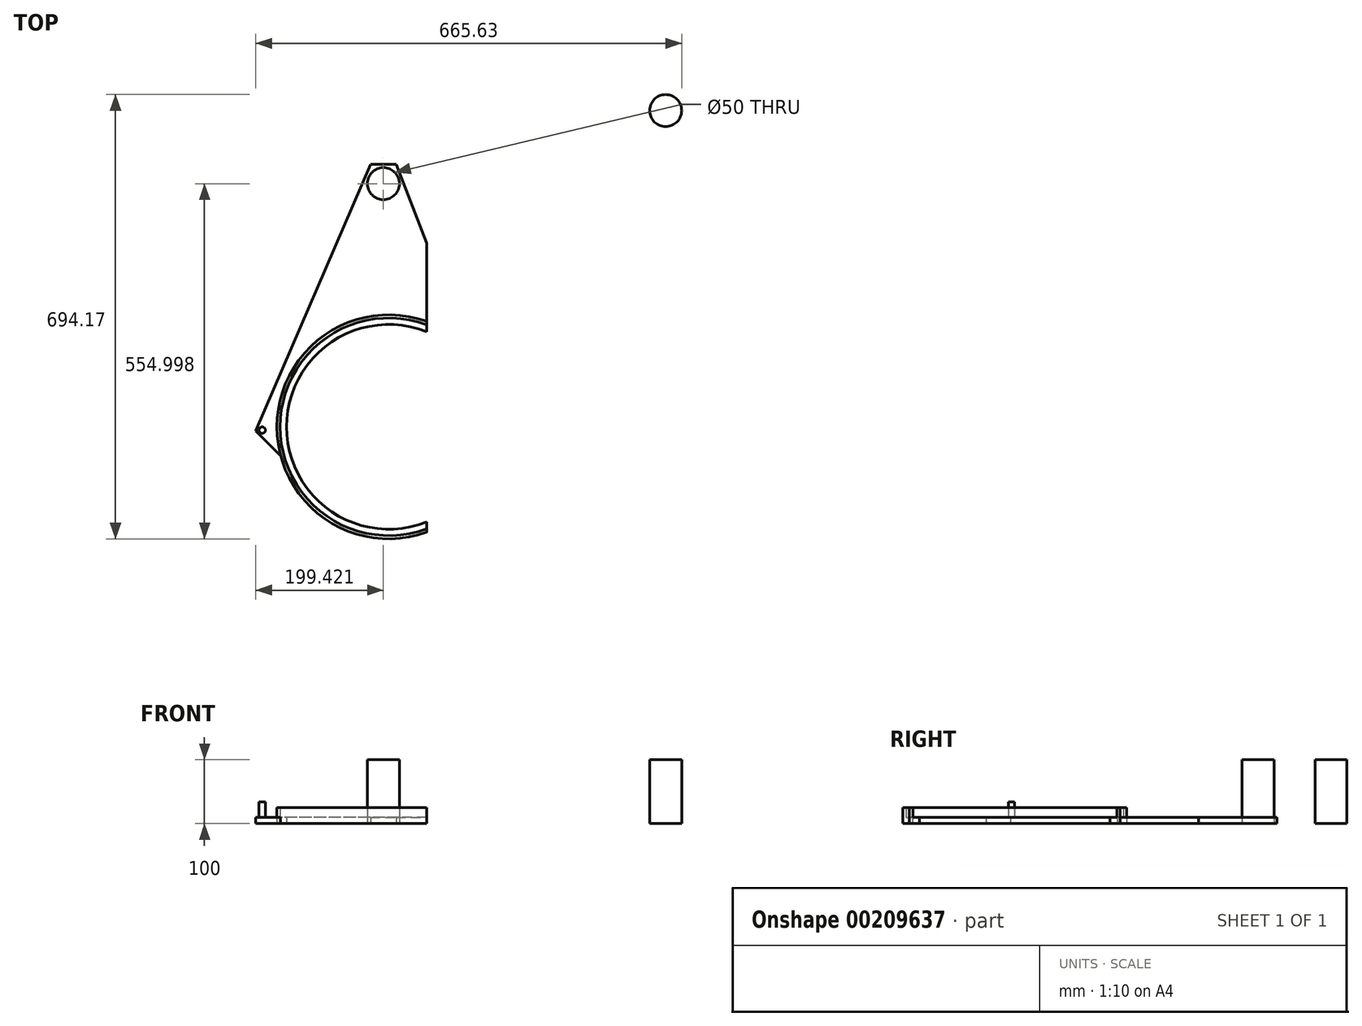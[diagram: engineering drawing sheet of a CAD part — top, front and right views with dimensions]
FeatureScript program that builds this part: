
annotation { "Feature Type Name" : "Feature", "Feature Type Description" : "" }
export const myFeature = defineFeature(function(context is Context, id is Id, definition is map)
    precondition{}
    {
        {
            var Q0;
            Q0=qCreatedBy(makeId("Top.planeOp"),FACE);
            var sketch = newSketch(context, id + "F0", { "sketchPlane" : qUnion([Q0])});
            skCircle(sketch, "E0", {"center": v(561.16, 574.84) * mm, "radius": 175 * mm});
            skCircle(sketch, "E1", {"center": v(561.16, 574.84) * mm, "radius": 160 * mm});
            skLineSegment(sketch, "E2", {"start": v(386.16, 574.84) * mm, "end": v(386.16, 644.84) * mm});
            skCircle(sketch, "E3", {"center": v(561.16, 574.84) * mm, "radius": 170 * mm});
            skLineSegment(sketch, "E4", {"start": v(532.63, 984.84) * mm, "end": v(572.63, 984.84) * mm});
            skCircle(sketch, "E5", {"center": v(552.63, 954.84) * mm, "radius": 25 * mm});
            skPoint(sketch, "E5.centerSnap0", {"position": v(552.63, 984.84) * mm});
            skPoint(sketch, "E6", {"position": v(386.16, 644.84) * mm});
            skPoint(sketch, "E7", {"position": v(727.63, 644.84) * mm});
            skLineSegment(sketch, "E8", {"start": v(532.63, 990.61) * mm, "end": v(572.63, 990.61) * mm, "construction": true});
            skPoint(sketch, "E9", {"position": v(552.63, 990.61) * mm});
            skPoint(sketch, "E10", {"position": v(532.63, 984.84) * mm});
            skPoint(sketch, "E11", {"position": v(572.63, 984.84) * mm});
            skLineSegment(sketch, "E12", {"start": v(386.16, 644.84) * mm, "end": v(532.63, 984.84) * mm});
            skPoint(sketch, "E13.orphan", {"position": v(719.1, 984.84) * mm});
            skPoint(sketch, "E14.orphan", {"position": v(386.16, 984.84) * mm});
            skPoint(sketch, "E15.centerSnap0", {"position": v(650.49, 644.84) * mm});
            skCircle(sketch, "E16", {"center": v(363.2, 569.67) * mm, "radius": 5 * mm});
            skLineSegment(sketch, "E17", {"start": v(386.16, 644.84) * mm, "end": v(350.06, 561.02) * mm});
            skLineSegment(sketch, "E18", {"start": v(353.21, 568.35) * mm, "end": v(392.04, 529.87) * mm});
            skPoint(sketch, "E19.start.orphan", {"position": v(736.16, 574.84) * mm});
            skLineSegment(sketch, "E20", {"start": v(572.63, 984.84) * mm, "end": v(620.08, 861.8) * mm});
            skLineSegment(sketch, "E21", {"start": v(620.08, 861.8) * mm, "end": v(620.08, 739.62) * mm});
            skLineSegment(sketch, "E22", {"start": v(620.08, 739.62) * mm, "end": v(620.08, 723.6) * mm});
            skLineSegment(sketch, "E23", {"start": v(620.08, 426.08) * mm, "end": v(620.08, 410.05) * mm});
            skCircle(sketch, "E24", {"center": v(993.84, 1069) * mm, "radius": 25 * mm});
            skSolve(sketch);
        }
        {
            var Q0;
            {var subQ0=sQuery(id+"F0.wireOp",EDGE,"E22");var subQ1=sQuery(id+"F0.wireOp",EDGE,"E1");var subQ2=makeQuery(id+"F0.imprint","INTERSECT",VERTEX,{"derivedFrom":[subQ1,subQ0]});Q0=makeQuery(id+"F0.imprint","IMPRINT",FACE,{"disambiguationData":[TD([[makeQuery(id+"F0.imprint","IMPRINT",EDGE,{"disambiguationData":[TD([[subQ2,-1.0]])],"derivedFrom":subQ1}),-1.0]])]});}
            extrude(context, id + "F1", {"entities" : qUnion([Q0]), "depth" : 10 * mm});
        }
        {
            var Q0;
            {var subQ5=sQuery(id+"F0.wireOp",EDGE,"E0");var subQ6=makeQuery(id+"F0.imprint","INTERSECT",VERTEX,{"derivedFrom":[subQ5,sQuery(id+"F0.wireOp",EDGE,"E2")]});Q0=makeQuery(id+"F0.imprint","IMPRINT",FACE,{"disambiguationData":[TD([[makeQuery(id+"F0.imprint","IMPRINT",EDGE,{"disambiguationData":[TD([[subQ6,-1.0]])],"derivedFrom":subQ5}),1.0]])]});}
            extrude(context, id + "F2", {"entities" : qUnion([Q0]), "operationType" : NewBodyOperationType.ADD, "depth" : 25 * mm});
        }
        {
            var Q0;
            Q0=makeQuery(id+"F0.imprint","IMPRINT",FACE,{"disambiguationData":[TD([[makeQuery(id+"F0.imprint","IMPRINT",EDGE,{"derivedFrom":sQuery(id+"F0.wireOp",EDGE,"E5")}),1.0]])]});
            extrude(context, id + "F3", {"entities" : qUnion([Q0]), "depth" : 100 * mm});
        }
        {
            var Q0;
            {var subQ1=sQuery(id+"F0.wireOp",EDGE,"E19");Q0=makeQuery(id+"F0.imprint","IMPRINT",FACE,{"disambiguationData":[TD([[makeQuery(id+"F0.imprint","IMPRINT",EDGE,{"derivedFrom":subQ1}),1.0]])]});}
            var Q1;
            Q1=makeQuery(id+"F0.imprint","IMPRINT",FACE,{"disambiguationData":[TD([[makeQuery(id+"F0.imprint","IMPRINT",EDGE,{"derivedFrom":sQuery(id+"F0.wireOp",EDGE,"E2")}),1.0]])]});
            var Q2;
            {var subQ0=sQuery(id+"F0.wireOp",EDGE,"E2");Q2=makeQuery(id+"F0.imprint","IMPRINT",FACE,{"disambiguationData":[TD([[makeQuery(id+"F0.imprint","IMPRINT",EDGE,{"derivedFrom":subQ0}),-1.0]])]});}
            extrude(context, id + "F4", {"entities" : qUnion([Q0, Q1, Q2]), "depth" : 10 * mm});
        }
        {
            var Q0;
            Q0=makeQuery(id+"F0.imprint","IMPRINT",FACE,{"disambiguationData":[TD([[makeQuery(id+"F0.imprint","IMPRINT",EDGE,{"derivedFrom":sQuery(id+"F0.wireOp",EDGE,"E15")}),1.0]])]});
            var Q1;
            Q1=makeQuery(id+"F0.imprint","IMPRINT",FACE,{"disambiguationData":[TD([[makeQuery(id+"F0.imprint","IMPRINT",EDGE,{"derivedFrom":sQuery(id+"F0.wireOp",EDGE,"E16")}),1.0]])]});
            extrude(context, id + "F5", {"entities" : qUnion([Q0, Q1]), "operationType" : NewBodyOperationType.ADD, "depth" : 34 * mm});
        }
        {
            var Q0;
            Q0=makeQuery(id+"F0.imprint","IMPRINT",FACE,{"disambiguationData":[TD([[makeQuery(id+"F0.imprint","IMPRINT",EDGE,{"derivedFrom":sQuery(id+"F0.wireOp",EDGE,"E24")}),1.0]])]});
            extrude(context, id + "F6", {"entities" : qUnion([Q0]), "depth" : 100 * mm});
        }
    });
